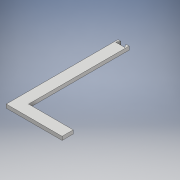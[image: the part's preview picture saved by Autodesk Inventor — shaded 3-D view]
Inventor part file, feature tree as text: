
AUTODESK INVENTOR PART (.ipt)
format: ipt  version: 2017 (Build 210142000, 142)  size: 112,128 bytes
history: native  units: mm
features: extrude x1, sketch x1
ambient origin geometry x8: Origin, YZ Plane, XZ Plane, XY Plane, X Axis, Y Axis, Z Axis, Center Point
bodies: Solid1 (feature_tree)
feature tree (2):
  extrude  "Extrusion1"  Depth=87.0mm
  sketch  "Sketch1"  dims[d0=10.0mm d1=45.0mm d2=100.0mm d3=45.0mm d4=5.0mm d5=50.0mm d6=3.175mm d7=0.0mm d8=3.0mm d9=4.0mm d12=120.0deg d13=4.0mm d14=60.0deg d15=45.0mm d16=87.0mm d17=33.744093mm]
